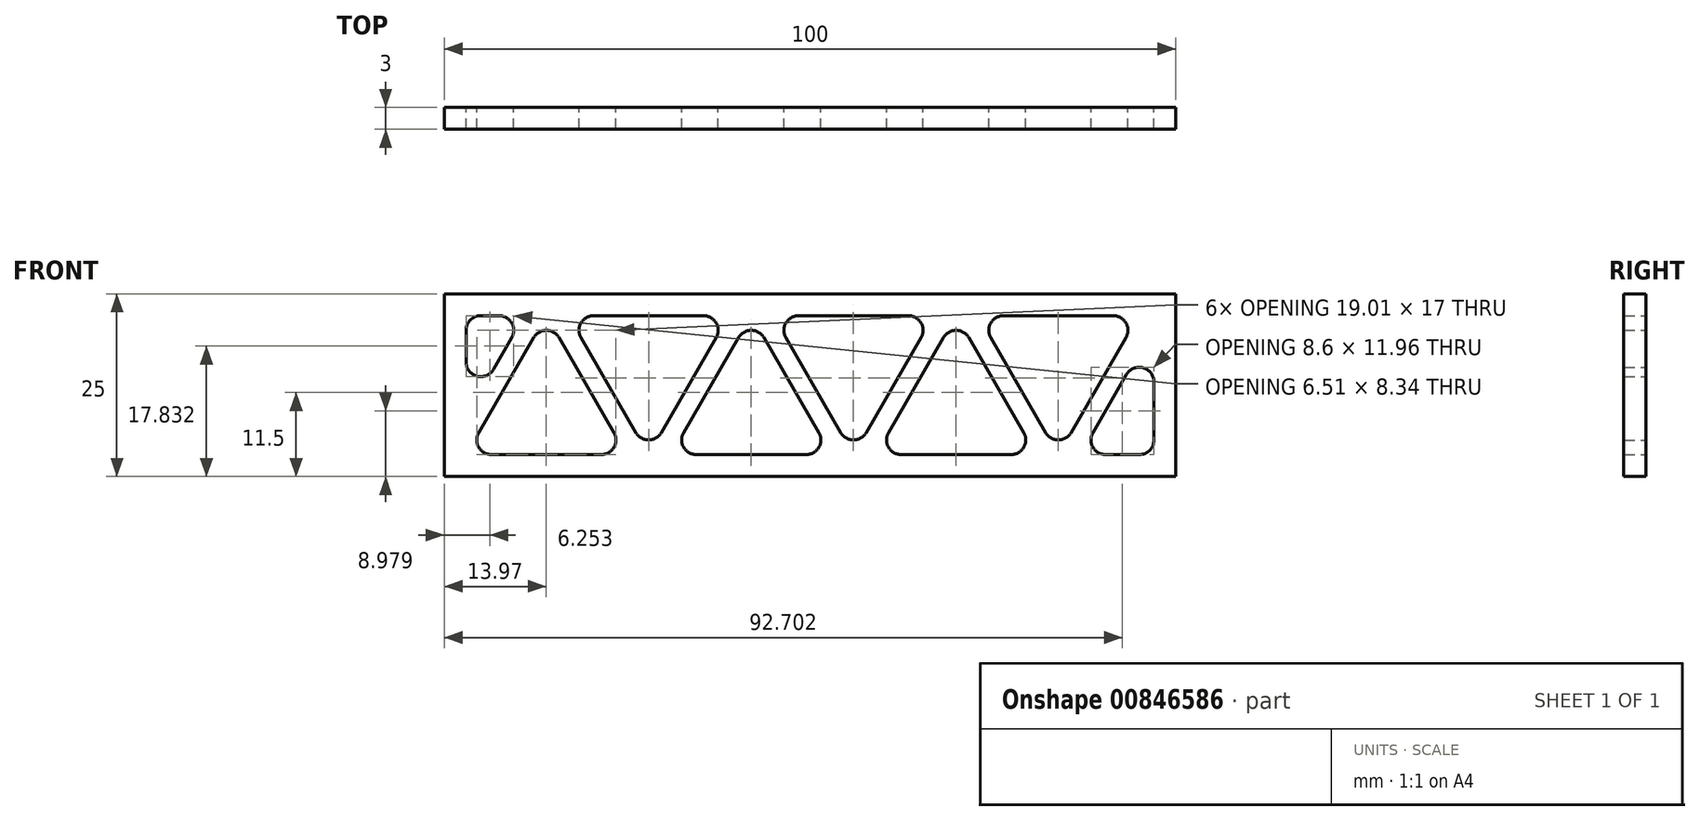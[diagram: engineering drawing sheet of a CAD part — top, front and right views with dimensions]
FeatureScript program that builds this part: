
annotation { "Feature Type Name" : "Feature", "Feature Type Description" : "" }
export const myFeature = defineFeature(function(context is Context, id is Id, definition is map)
    precondition{}
    {
        {
            var Q0;
            Q0=qCreatedBy(makeId("Front.planeOp"),FACE);
            var sketch = newSketch(context, id + "F0", { "sketchPlane" : qUnion([Q0])});
            skLineSegment(sketch, "E0.bottom", {"start": v(0, 0) * mm, "end": v(100, 0) * mm});
            skLineSegment(sketch, "E0.top", {"start": v(0, 25) * mm, "end": v(100, 25) * mm});
            skLineSegment(sketch, "E0.left", {"start": v(0, 0) * mm, "end": v(0, 25) * mm});
            skLineSegment(sketch, "E0.right", {"start": v(100, 0) * mm, "end": v(100, 25) * mm});
            skLineSegment(sketch, "E1", {"start": v(12.24, 19) * mm, "end": v(4.73, 6) * mm});
            skLineSegment(sketch, "E2", {"start": v(6.46, 3) * mm, "end": v(21.48, 3) * mm});
            skLineSegment(sketch, "E3", {"start": v(23.2, 6) * mm, "end": v(15.7, 19) * mm});
            skPoint(sketch, "E4.visualSharp", {"position": v(13.97, 22) * mm});
            skArc(sketch, "E4.filletArc", {"start": v(15.7, 19) * mm, "mid": v(13.97, 20) * mm, "end": v(12.24, 19) * mm});
            skPoint(sketch, "E5.visualSharp", {"position": v(24.94, 3) * mm});
            skArc(sketch, "E5.filletArc", {"start": v(21.48, 3) * mm, "mid": v(23.2, 4) * mm, "end": v(23.2, 6) * mm});
            skPoint(sketch, "E6.visualSharp", {"position": v(3, 3) * mm});
            skArc(sketch, "E6.filletArc", {"start": v(4.73, 6) * mm, "mid": v(4.73, 4) * mm, "end": v(6.46, 3) * mm});
            skLineSegment(sketch, "E7", {"start": v(18.7, 19) * mm, "end": v(26.2, 6) * mm});
            skLineSegment(sketch, "E8", {"start": v(29.67, 6) * mm, "end": v(37.18, 19) * mm});
            skLineSegment(sketch, "E9", {"start": v(35.44, 22) * mm, "end": v(20.43, 22) * mm});
            skPoint(sketch, "E10.visualSharp", {"position": v(16.97, 22) * mm});
            skArc(sketch, "E10.filletArc", {"start": v(20.43, 22) * mm, "mid": v(18.7, 21) * mm, "end": v(18.7, 19) * mm});
            skPoint(sketch, "E11.visualSharp", {"position": v(38.9, 22) * mm});
            skArc(sketch, "E11.filletArc", {"start": v(37.18, 19) * mm, "mid": v(37.18, 21) * mm, "end": v(35.44, 22) * mm});
            skPoint(sketch, "E12.visualSharp", {"position": v(27.94, 3) * mm});
            skArc(sketch, "E12.filletArc", {"start": v(26.2, 6) * mm, "mid": v(27.94, 5) * mm, "end": v(29.67, 6) * mm});
            skPoint(sketch, "E13.1.0.0", {"position": v(52.94, 3) * mm});
            skArc(sketch, "E13.1.0.1", {"start": v(49.48, 3) * mm, "mid": v(51.2, 4) * mm, "end": v(51.2, 6) * mm});
            skLineSegment(sketch, "E13.1.0.2", {"start": v(57.67, 6) * mm, "end": v(65.18, 19) * mm});
            skLineSegment(sketch, "E13.1.0.3", {"start": v(46.7, 19) * mm, "end": v(54.2, 6) * mm});
            skArc(sketch, "E13.1.0.4", {"start": v(54.2, 6) * mm, "mid": v(55.94, 5) * mm, "end": v(57.67, 6) * mm});
            skPoint(sketch, "E13.1.0.5", {"position": v(41.97, 22) * mm});
            skPoint(sketch, "E13.1.0.6", {"position": v(44.97, 22) * mm});
            skArc(sketch, "E13.1.0.7", {"start": v(32.73, 6) * mm, "mid": v(32.73, 4) * mm, "end": v(34.46, 3) * mm});
            skLineSegment(sketch, "E13.1.0.8", {"start": v(51.2, 6) * mm, "end": v(43.7, 19) * mm});
            skPoint(sketch, "E13.1.0.9", {"position": v(66.9, 22) * mm});
            skArc(sketch, "E13.1.0.10", {"start": v(65.18, 19) * mm, "mid": v(65.18, 21) * mm, "end": v(63.44, 22) * mm});
            skLineSegment(sketch, "E13.1.0.11", {"start": v(40.24, 19) * mm, "end": v(32.73, 6) * mm});
            skArc(sketch, "E13.1.0.12", {"start": v(48.43, 22) * mm, "mid": v(46.7, 21) * mm, "end": v(46.7, 19) * mm});
            skLineSegment(sketch, "E13.1.0.13", {"start": v(34.46, 3) * mm, "end": v(49.48, 3) * mm});
            skArc(sketch, "E13.1.0.14", {"start": v(43.7, 19) * mm, "mid": v(41.97, 20) * mm, "end": v(40.24, 19) * mm});
            skPoint(sketch, "E13.1.0.15", {"position": v(31, 3) * mm});
            skPoint(sketch, "E13.1.0.16", {"position": v(55.94, 3) * mm});
            skLineSegment(sketch, "E13.1.0.17", {"start": v(63.44, 22) * mm, "end": v(48.43, 22) * mm});
            skPoint(sketch, "E13.2.0.0", {"position": v(80.94, 3) * mm});
            skArc(sketch, "E13.2.0.1", {"start": v(77.48, 3) * mm, "mid": v(79.2, 4) * mm, "end": v(79.2, 6) * mm});
            skLineSegment(sketch, "E13.2.0.2", {"start": v(85.67, 6) * mm, "end": v(93.18, 19) * mm});
            skLineSegment(sketch, "E13.2.0.3", {"start": v(74.7, 19) * mm, "end": v(82.2, 6) * mm});
            skArc(sketch, "E13.2.0.4", {"start": v(82.2, 6) * mm, "mid": v(83.94, 5) * mm, "end": v(85.67, 6) * mm});
            skPoint(sketch, "E13.2.0.5", {"position": v(69.97, 22) * mm});
            skPoint(sketch, "E13.2.0.6", {"position": v(72.97, 22) * mm});
            skArc(sketch, "E13.2.0.7", {"start": v(60.73, 6) * mm, "mid": v(60.73, 4) * mm, "end": v(62.46, 3) * mm});
            skLineSegment(sketch, "E13.2.0.8", {"start": v(79.2, 6) * mm, "end": v(71.7, 19) * mm});
            skPoint(sketch, "E13.2.0.9", {"position": v(94.9, 22) * mm});
            skArc(sketch, "E13.2.0.10", {"start": v(93.18, 19) * mm, "mid": v(93.18, 21) * mm, "end": v(91.44, 22) * mm});
            skLineSegment(sketch, "E13.2.0.11", {"start": v(68.24, 19) * mm, "end": v(60.73, 6) * mm});
            skArc(sketch, "E13.2.0.12", {"start": v(76.43, 22) * mm, "mid": v(74.7, 21) * mm, "end": v(74.7, 19) * mm});
            skLineSegment(sketch, "E13.2.0.13", {"start": v(62.46, 3) * mm, "end": v(77.48, 3) * mm});
            skArc(sketch, "E13.2.0.14", {"start": v(71.7, 19) * mm, "mid": v(69.97, 20) * mm, "end": v(68.24, 19) * mm});
            skPoint(sketch, "E13.2.0.15", {"position": v(59, 3) * mm});
            skPoint(sketch, "E13.2.0.16", {"position": v(83.94, 3) * mm});
            skLineSegment(sketch, "E13.2.0.17", {"start": v(91.44, 22) * mm, "end": v(76.43, 22) * mm});
            skLineSegment(sketch, "E13.direction1", {"start": v(3, 3) * mm, "end": v(31, 3) * mm, "construction": true});
            skLineSegment(sketch, "E14", {"start": v(5, 22) * mm, "end": v(7.5, 22) * mm});
            skLineSegment(sketch, "E15", {"start": v(9.24, 19) * mm, "end": v(6.73, 14.66) * mm});
            skLineSegment(sketch, "E16", {"start": v(3, 15.66) * mm, "end": v(3, 20) * mm});
            skPoint(sketch, "E17.visualSharp", {"position": v(3, 22) * mm});
            skArc(sketch, "E17.filletArc", {"start": v(5, 22) * mm, "mid": v(3.59, 21.41) * mm, "end": v(3, 20) * mm});
            skPoint(sketch, "E18.visualSharp", {"position": v(10.97, 22) * mm});
            skArc(sketch, "E18.filletArc", {"start": v(9.24, 19) * mm, "mid": v(9.24, 21) * mm, "end": v(7.5, 22) * mm});
            skPoint(sketch, "E19.visualSharp", {"position": v(3, 8.2) * mm});
            skArc(sketch, "E19.filletArc", {"start": v(3, 15.66) * mm, "mid": v(4.48, 13.73) * mm, "end": v(6.73, 14.66) * mm});
            skLineSegment(sketch, "E20", {"start": v(97, 5) * mm, "end": v(97, 12.96) * mm});
            skLineSegment(sketch, "E21", {"start": v(93.27, 13.96) * mm, "end": v(88.67, 6) * mm});
            skLineSegment(sketch, "E22", {"start": v(90.4, 3) * mm, "end": v(95, 3) * mm});
            skPoint(sketch, "E23.visualSharp", {"position": v(97, 20.43) * mm});
            skArc(sketch, "E23.filletArc", {"start": v(97, 12.96) * mm, "mid": v(95.52, 14.9) * mm, "end": v(93.27, 13.96) * mm});
            skPoint(sketch, "E24.visualSharp", {"position": v(97, 3) * mm});
            skArc(sketch, "E24.filletArc", {"start": v(95, 3) * mm, "mid": v(96.41, 3.59) * mm, "end": v(97, 5) * mm});
            skPoint(sketch, "E25.visualSharp", {"position": v(86.94, 3) * mm});
            skArc(sketch, "E25.filletArc", {"start": v(88.67, 6) * mm, "mid": v(88.67, 4) * mm, "end": v(90.4, 3) * mm});
            skSolve(sketch);
        }
        {
            var Q0;
            Q0=makeQuery(id+"F0.imprint","IMPRINT",FACE,{"disambiguationData":[TD([[makeQuery(id+"F0.imprint","IMPRINT",EDGE,{"derivedFrom":sQuery(id+"F0.wireOp",EDGE,"E0.bottom")}),1.0]])]});
            extrude(context, id + "F1", {"entities" : qUnion([Q0]), "depth" : 3 * mm, "offsetDistance" : 25 * mm});
        }
    });
